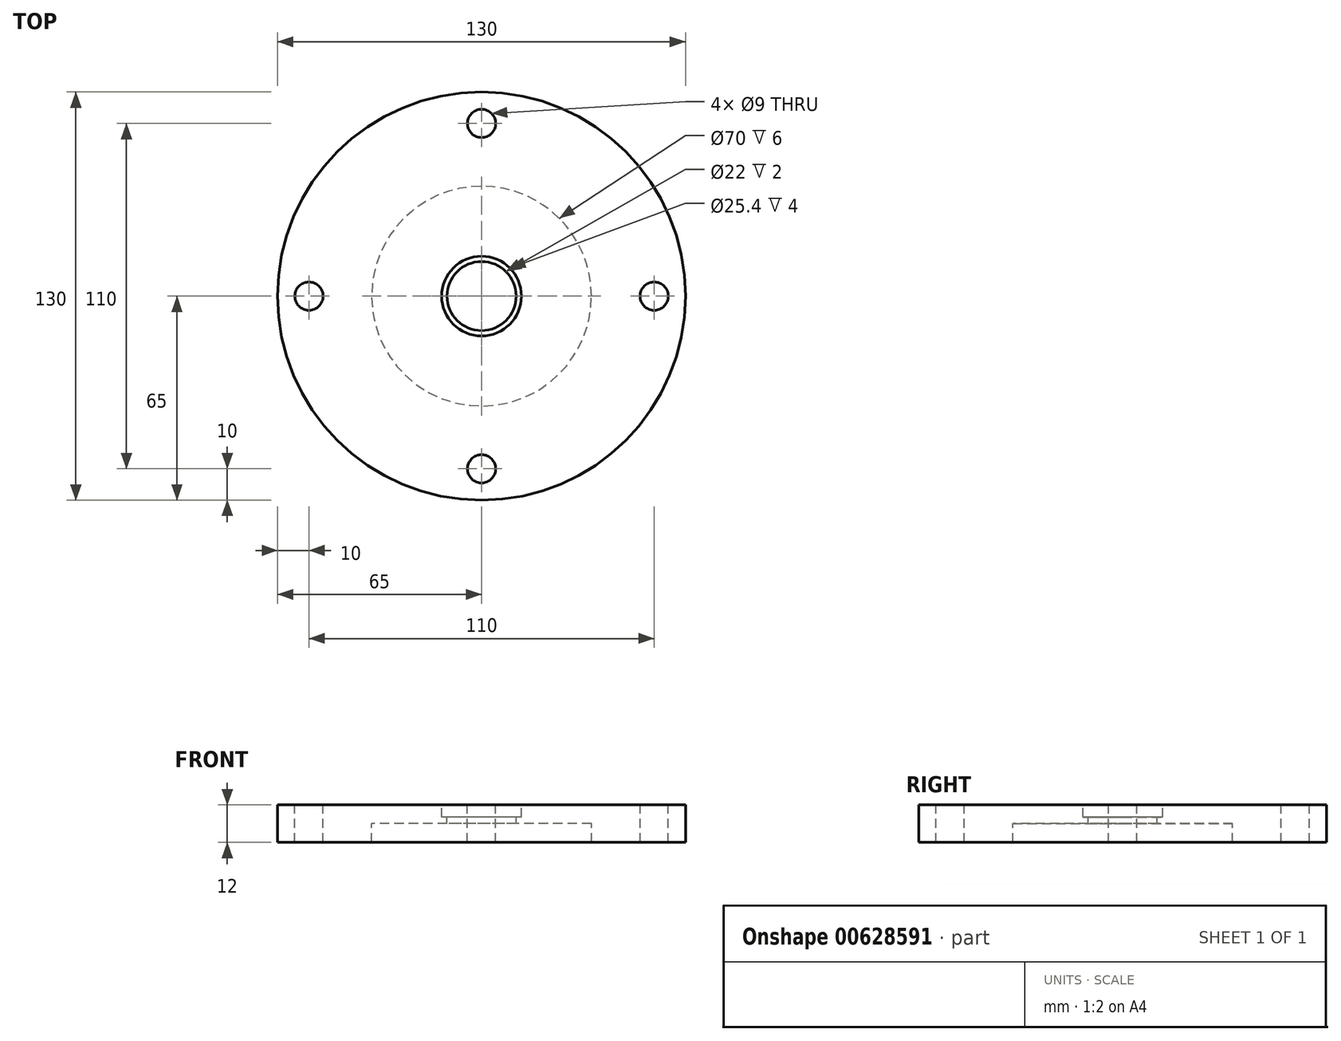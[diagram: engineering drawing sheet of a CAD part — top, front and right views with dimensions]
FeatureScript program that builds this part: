
annotation { "Feature Type Name" : "Feature", "Feature Type Description" : "" }
export const myFeature = defineFeature(function(context is Context, id is Id, definition is map)
    precondition{}
    {
        {
            var Q0;
            Q0=qCreatedBy(makeId("Front.planeOp"),FACE);
            var sketch = newSketch(context, id + "F0", { "sketchPlane" : qUnion([Q0])});
            skLineSegment(sketch, "E0", {"start": v(0, 0) * mm, "end": v(0, 36.91) * mm, "construction": true});
            skLineSegment(sketch, "E1.bottom", {"start": v(0, 0) * mm, "end": v(65, 0) * mm});
            skLineSegment(sketch, "E1.top", {"start": v(0, 12) * mm, "end": v(65, 12) * mm});
            skLineSegment(sketch, "E1.left", {"start": v(0, 0) * mm, "end": v(0, 12) * mm});
            skLineSegment(sketch, "E1.right", {"start": v(65, 0) * mm, "end": v(65, 12) * mm});
            skSolve(sketch);
        }
        {
            var Q0;
            Q0 = qSketchRegion(id + "F0", true);
            var Q1;
            Q1=sQuery(id+"F0.wireOp",EDGE,"E0");
            revolve(context, id + "F1", {"entities" : qUnion([Q0]), "axis" : qUnion([Q1]), "revolveType" : RevolveType.FULL});
        }
        {
            var Q0;
            Q0=qCreatedBy(makeId("Front.planeOp"),FACE);
            var sketch = newSketch(context, id + "F2", { "sketchPlane" : qUnion([Q0])});
            skLineSegment(sketch, "E2", {"start": v(0, 0) * mm, "end": v(35, 0) * mm});
            skLineSegment(sketch, "E3", {"start": v(35, 0) * mm, "end": v(35, 6) * mm});
            skLineSegment(sketch, "E4", {"start": v(35, 6) * mm, "end": v(11, 6) * mm});
            skLineSegment(sketch, "E5", {"start": v(11, 6) * mm, "end": v(11, 8) * mm});
            skLineSegment(sketch, "E6", {"start": v(11, 8) * mm, "end": v(12.7, 8) * mm});
            skLineSegment(sketch, "E7.0", {"start": v(12.7, 12) * mm, "end": v(0, 12) * mm});
            skLineSegment(sketch, "E8", {"start": v(12.7, 8) * mm, "end": v(12.7, 12) * mm});
            skPoint(sketch, "E9.orphan", {"position": v(-65, 12) * mm});
            skLineSegment(sketch, "E10", {"start": v(0, 0) * mm, "end": v(0, 22.54) * mm, "construction": true});
            skLineSegment(sketch, "E11", {"start": v(0, 12) * mm, "end": v(0, 0) * mm});
            skPoint(sketch, "E12.orphan", {"position": v(65, 12) * mm});
            skSolve(sketch);
        }
        {
            var Q0;
            Q0 = qSketchRegion(id + "F2", true);
            var Q1;
            Q1=sQuery(id+"F2.wireOp",EDGE,"E10");
            revolve(context, id + "F3", {"operationType" : NewBodyOperationType.REMOVE, "entities" : qUnion([Q0]), "axis" : qUnion([Q1]), "revolveType" : RevolveType.FULL, "oppositeDirection" : true});
        }
        {
            var Q0;
            Q0=makeQuery(id+"F1.opRevolve","SWEPT_FACE",FACE,{"disambiguationData":[OSD([sQuery(id+"F0.wireOp",EDGE,"E1.top")])]});
            var sketch = newSketch(context, id + "F4", { "sketchPlane" : qUnion([Q0])});
            skLineSegment(sketch, "E13", {"start": v(0, 0) * mm, "end": v(79.6, 0) * mm, "construction": true});
            skLineSegment(sketch, "E14", {"start": v(0, 0) * mm, "end": v(0, 79.85) * mm, "construction": true});
            skCircle(sketch, "E15", {"center": v(0, 0) * mm, "radius": 55 * mm, "construction": true});
            skCircle(sketch, "E16", {"center": v(55, 0) * mm, "radius": 4.5 * mm});
            skCircle(sketch, "E17", {"center": v(0, 55) * mm, "radius": 4.5 * mm});
            skCircle(sketch, "E18.MirrorC", {"center": v(-55, 0) * mm, "radius": 4.5 * mm});
            skCircle(sketch, "E19.MirrorC", {"center": v(0, -55) * mm, "radius": 4.5 * mm});
            skSolve(sketch);
        }
        {
            var Q0;
            Q0 = qSketchRegion(id + "F4", true);
            extrude(context, id + "F5", {"entities" : qUnion([Q0]), "operationType" : NewBodyOperationType.REMOVE, "endBound" : BoundingType.UP_TO_NEXT, "oppositeDirection" : true, "depth" : 25 * mm, "offsetDistance" : 25 * mm});
        }
    });
